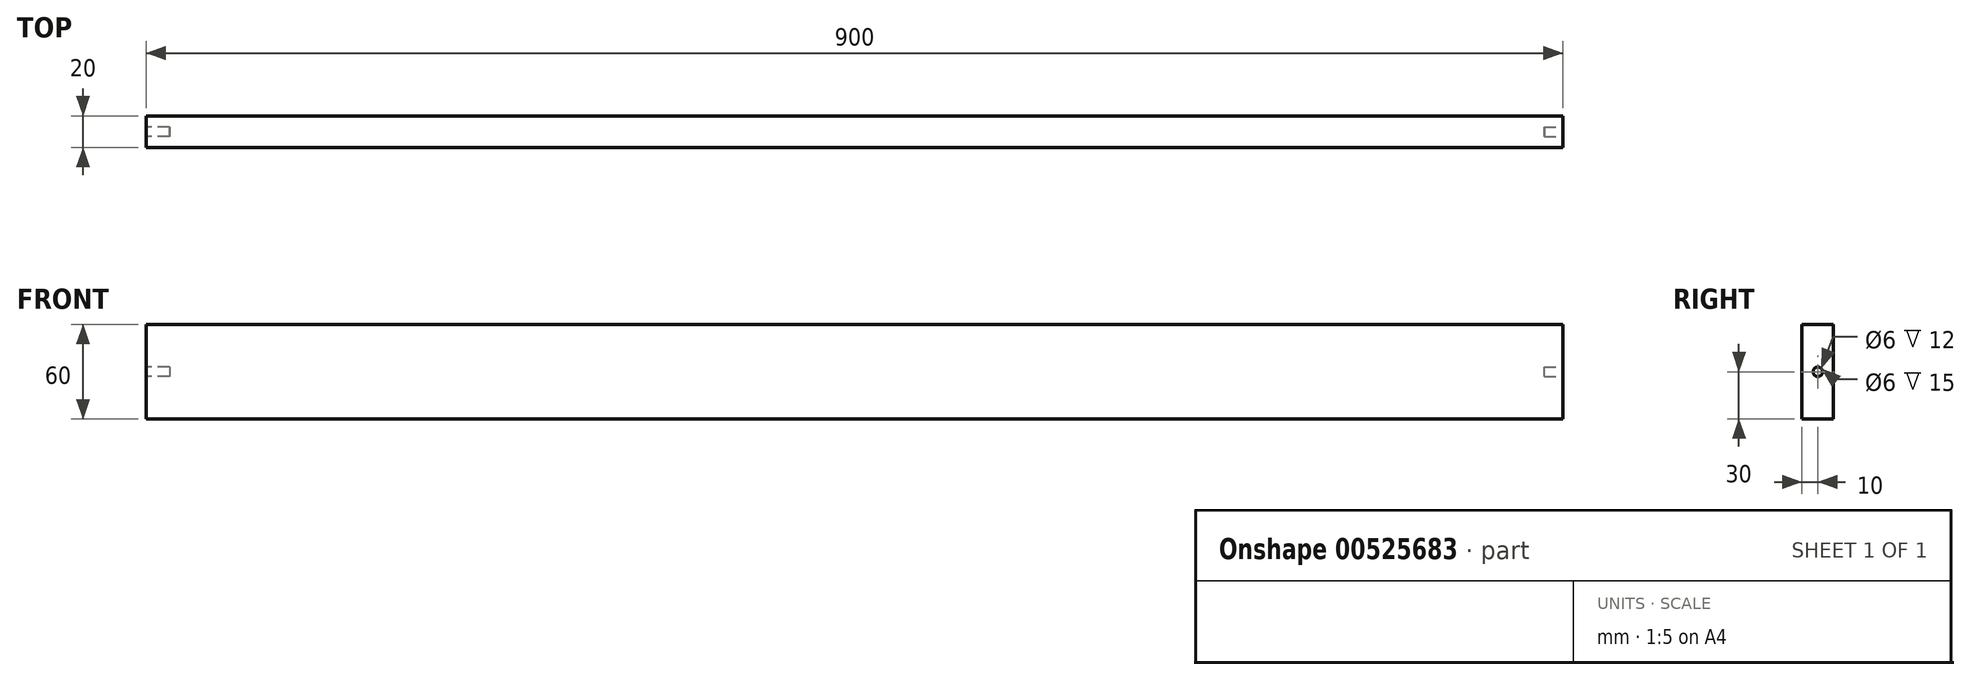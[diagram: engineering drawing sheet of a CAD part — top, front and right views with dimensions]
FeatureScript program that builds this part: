
annotation { "Feature Type Name" : "Feature", "Feature Type Description" : "" }
export const myFeature = defineFeature(function(context is Context, id is Id, definition is map)
    precondition{}
    {
        {
            var Q0;
            Q0=qCreatedBy(makeId("Right.planeOp"),FACE);
            var sketch = newSketch(context, id + "F0", { "sketchPlane" : qUnion([Q0])});
            skLineSegment(sketch, "E0.bottom", {"start": v(0, 0) * mm, "end": v(20, 0) * mm});
            skLineSegment(sketch, "E0.top", {"start": v(0, 60) * mm, "end": v(20, 60) * mm});
            skLineSegment(sketch, "E0.left", {"start": v(0, 0) * mm, "end": v(0, 60) * mm});
            skLineSegment(sketch, "E0.right", {"start": v(20, 0) * mm, "end": v(20, 60) * mm});
            skSolve(sketch);
        }
        {
            var Q0;
            Q0=qSketchRegion(id+"F0",true);
            extrude(context, id + "F1", {"entities" : qUnion([Q0]), "depth" : 900 * mm, "offsetDistance" : 25 * mm, "symmetric" : true});
        }
        {
            var Q0;
            Q0=makeQuery(id+"F1.opExtrude","CAP_FACE",FACE,{"disambiguationData":[OSD([sQuery(id+"F0.wireOp",EDGE,"E0.bottom"),sQuery(id+"F0.wireOp",EDGE,"E0.top"),sQuery(id+"F0.wireOp",EDGE,"E0.left"),sQuery(id+"F0.wireOp",EDGE,"E0.right")])],"isStart":false});
            var sketch = newSketch(context, id + "F2", { "sketchPlane" : qUnion([Q0])});
            skCircle(sketch, "E1", {"center": v(10, 30) * mm, "radius": 3 * mm});
            skPoint(sketch, "E1.centerSnap0", {"position": v(0, 30) * mm});
            skPoint(sketch, "E1.centerSnap1", {"position": v(10, 60) * mm});
            skSolve(sketch);
        }
        {
            var Q0;
            Q0=qSketchRegion(id+"F2",true);
            extrude(context, id + "F3", {"entities" : qUnion([Q0]), "operationType" : NewBodyOperationType.REMOVE, "oppositeDirection" : true, "depth" : 12 * mm, "offsetDistance" : 25 * mm});
        }
        {
            var Q0;
            Q0=makeQuery(id+"F1.opExtrude","CAP_FACE",FACE,{"disambiguationData":[OSD([sQuery(id+"F0.wireOp",EDGE,"E0.bottom"),sQuery(id+"F0.wireOp",EDGE,"E0.top"),sQuery(id+"F0.wireOp",EDGE,"E0.left"),sQuery(id+"F0.wireOp",EDGE,"E0.right")])],"isStart":true});
            var sketch = newSketch(context, id + "F4", { "sketchPlane" : qUnion([Q0])});
            skSolve(sketch);
        }
        {
            var Q0;
            Q0=makeQuery(id+"F4.imprint","IMPRINT",FACE,{"disambiguationData":[TD([[makeQuery(id+"F4.imprint","IMPRINT",EDGE,{"derivedFrom":makeQuery(id+"F1.opExtrude","CAP_EDGE",EDGE,{"disambiguationData":[OSD([sQuery(id+"F0.wireOp",EDGE,"E0.bottom")])],"isStart":true})}),-1.0]])]});
            var sketch = newSketch(context, id + "F5", { "sketchPlane" : qUnion([Q0])});
            skCircle(sketch, "E2", {"center": v(-10, 30) * mm, "radius": 3 * mm});
            skSolve(sketch);
        }
        {
            var Q0;
            Q0=makeQuery(id+"F5.imprint","IMPRINT",FACE,{"disambiguationData":[TD([[makeQuery(id+"F5.imprint","IMPRINT",EDGE,{"derivedFrom":sQuery(id+"F5.wireOp",EDGE,"E2")}),1.0]])]});
            extrude(context, id + "F6", {"entities" : qUnion([Q0]), "operationType" : NewBodyOperationType.REMOVE, "oppositeDirection" : true, "depth" : 15 * mm, "offsetDistance" : 25 * mm});
        }
    });
